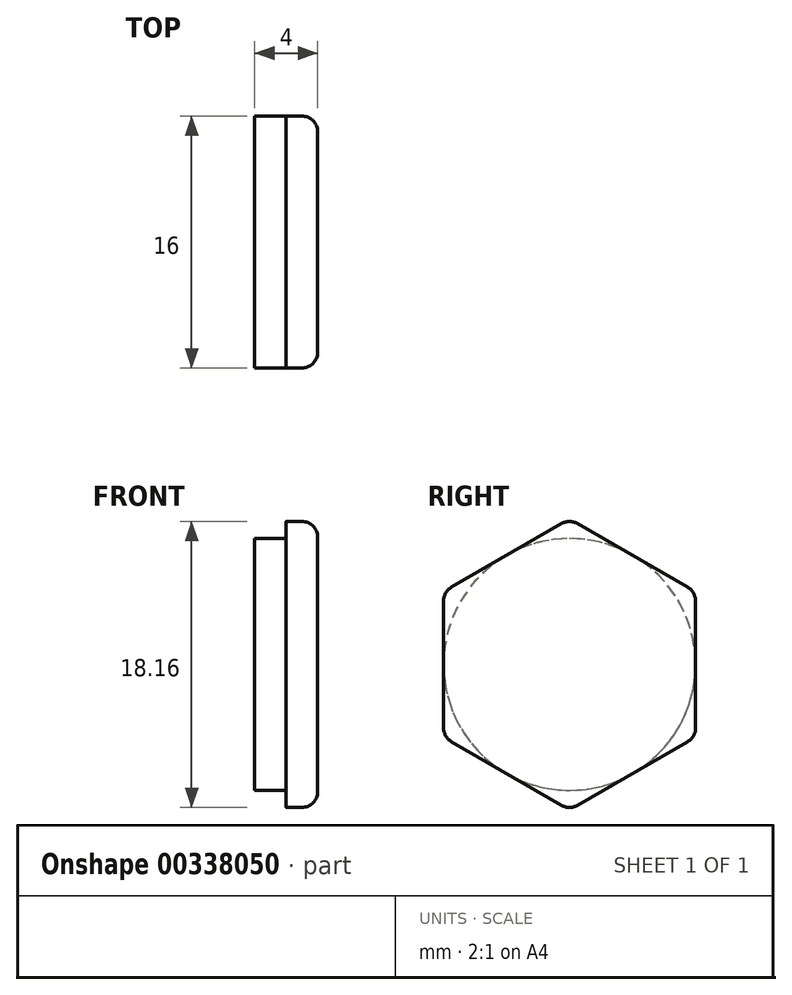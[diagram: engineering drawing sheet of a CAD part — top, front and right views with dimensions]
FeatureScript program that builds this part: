
annotation { "Feature Type Name" : "Feature", "Feature Type Description" : "" }
export const myFeature = defineFeature(function(context is Context, id is Id, definition is map)
    precondition{}
    {
        {
            var Q0;
            Q0=qCreatedBy(makeId("Right.planeOp"),FACE);
            var sketch = newSketch(context, id + "F0", { "sketchPlane" : qUnion([Q0])});
            skCircle(sketch, "E0", {"center": v(0, 0) * mm, "radius": 8 * mm});
            skSolve(sketch);
        }
        {
            var Q0;
            Q0=qSketchRegion(id+"F0",true);
            extrude(context, id + "F1", {"entities" : qUnion([Q0]), "depth" : 2 * mm});
        }
        {
            var Q0;
            Q0=makeQuery(id+"F1.opExtrude","CAP_FACE",FACE,{"disambiguationData":[OSD([sQuery(id+"F0.wireOp",EDGE,"E0")])],"isStart":false});
            var sketch = newSketch(context, id + "F2", { "sketchPlane" : qUnion([Q0])});
            skCircle(sketch, "E1.cCircle", {"center": v(0, 0) * mm, "radius": 8 * mm, "construction": true});
            skLineSegment(sketch, "E1.0", {"start": v(8, 4.62) * mm, "end": v(8, -4.62) * mm});
            skLineSegment(sketch, "E1.1", {"start": v(8, -4.62) * mm, "end": v(0, -9.24) * mm});
            skLineSegment(sketch, "E1.2", {"start": v(0, -9.24) * mm, "end": v(-8, -4.62) * mm});
            skLineSegment(sketch, "E1.3", {"start": v(-8, -4.62) * mm, "end": v(-8, 4.62) * mm});
            skLineSegment(sketch, "E1.4", {"start": v(-8, 4.62) * mm, "end": v(0, 9.24) * mm});
            skLineSegment(sketch, "E1.5", {"start": v(0, 9.24) * mm, "end": v(8, 4.62) * mm});
            skPoint(sketch, "E1.0.midPoint", {"position": v(8, 0) * mm});
            skSolve(sketch);
        }
        {
            var Q0;
            Q0=qSketchRegion(id+"F2",true);
            extrude(context, id + "F3", {"entities" : qUnion([Q0]), "operationType" : NewBodyOperationType.ADD, "depth" : 2 * mm});
        }
        {
            var Q0;
            Q0=makeQuery(id+"F3.opExtrude","SWEPT_EDGE",EDGE,{"disambiguationData":[OSD([sQuery(id+"F2.wireOp",EDGE,"E1.4"),sQuery(id+"F2.wireOp",EDGE,"E1.5")])]});
            var Q1;
            Q1=makeQuery(id+"F3.opExtrude","SWEPT_EDGE",EDGE,{"disambiguationData":[OSD([sQuery(id+"F2.wireOp",EDGE,"E1.0"),sQuery(id+"F2.wireOp",EDGE,"E1.5")])]});
            var Q2;
            Q2=makeQuery(id+"F3.opExtrude","SWEPT_EDGE",EDGE,{"disambiguationData":[OSD([sQuery(id+"F2.wireOp",EDGE,"E1.0"),sQuery(id+"F2.wireOp",EDGE,"E1.1")])]});
            var Q3;
            Q3=makeQuery(id+"F3.opExtrude","SWEPT_EDGE",EDGE,{"disambiguationData":[OSD([sQuery(id+"F2.wireOp",EDGE,"E1.3"),sQuery(id+"F2.wireOp",EDGE,"E1.4")])]});
            var Q4;
            Q4=makeQuery(id+"F3.opExtrude","SWEPT_EDGE",EDGE,{"disambiguationData":[OSD([sQuery(id+"F2.wireOp",EDGE,"E1.2"),sQuery(id+"F2.wireOp",EDGE,"E1.3")])]});
            var Q5;
            Q5=makeQuery(id+"F3.opExtrude","SWEPT_EDGE",EDGE,{"disambiguationData":[OSD([sQuery(id+"F2.wireOp",EDGE,"E1.1"),sQuery(id+"F2.wireOp",EDGE,"E1.2")])]});
            var Q6;
            Q6=makeQuery(id+"F3.opExtrude","CAP_EDGE",EDGE,{"disambiguationData":[OSD([sQuery(id+"F2.wireOp",EDGE,"E1.4")])],"isStart":false});
            var Q7;
            Q7=makeQuery(id+"F3.opExtrude","CAP_EDGE",EDGE,{"disambiguationData":[OSD([sQuery(id+"F2.wireOp",EDGE,"E1.3")])],"isStart":false});
            var Q8;
            Q8=makeQuery(id+"F3.opExtrude","CAP_EDGE",EDGE,{"disambiguationData":[OSD([sQuery(id+"F2.wireOp",EDGE,"E1.2")])],"isStart":false});
            var Q9;
            Q9=makeQuery(id+"F3.opExtrude","CAP_EDGE",EDGE,{"disambiguationData":[OSD([sQuery(id+"F2.wireOp",EDGE,"E1.5")])],"isStart":false});
            var Q10;
            Q10=makeQuery(id+"F3.opExtrude","CAP_EDGE",EDGE,{"disambiguationData":[OSD([sQuery(id+"F2.wireOp",EDGE,"E1.0")])],"isStart":false});
            var Q11;
            Q11=makeQuery(id+"F3.opExtrude","CAP_EDGE",EDGE,{"disambiguationData":[OSD([sQuery(id+"F2.wireOp",EDGE,"E1.1")])],"isStart":false});
            fillet(context, id + "F4", {"entities" : qUnion([Q0, Q1, Q2, Q3, Q4, Q5, Q6, Q7, Q8, Q9, Q10, Q11]), "radius" : 1 * mm, "tangentPropagation" : true, "allowEdgeOverflow" : false});
        }
    });
